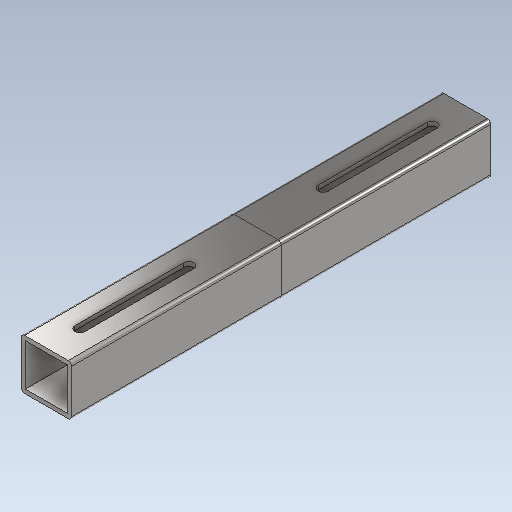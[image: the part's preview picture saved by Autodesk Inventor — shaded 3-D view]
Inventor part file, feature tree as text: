
AUTODESK INVENTOR PART (.ipt)
format: ipt  version: 2021 (Build 250183000, 183)  size: 252,928 bytes
history: native  units: mm
features: extrude x2, split x2, sketch x2, fillet x1, plane x1, other x1
ambient origin geometry x8: Origin, YZ Plane, XZ Plane, XY Plane, X Axis, Y Axis, Z Axis, Center Point
bodies: Solid1 (feature_tree), Solid4 (feature_tree), Solid5 (feature_tree)
feature tree (9):
  extrude  "Extrusion1"  Depth=30.0mm
  fillet  "Fillet1"  Radius=15.0mm
  plane  "Work Plane1"
  split  "Split1"
  other  "midPlane"
  extrude  "Extrusion2"  Depth=2.5mm
  split  "Split3"
  sketch  "Sketch1"  dims[d0=30.0mm d1=30.0mm d2=15.0mm]
  sketch  "Sketch3"  dims[d3=15.0mm d4=2.5mm d5=1000.0mm d6=0.0mm d7=2.0mm d8=-250.0mm d28=6.0mm d29=6.0mm d30=30.0mm d31=15.0mm d32=15.0mm d33=65.0mm d34=65.0mm d35=20.0mm d36=20.0mm d37=0.0mm d38=0.0mm]
